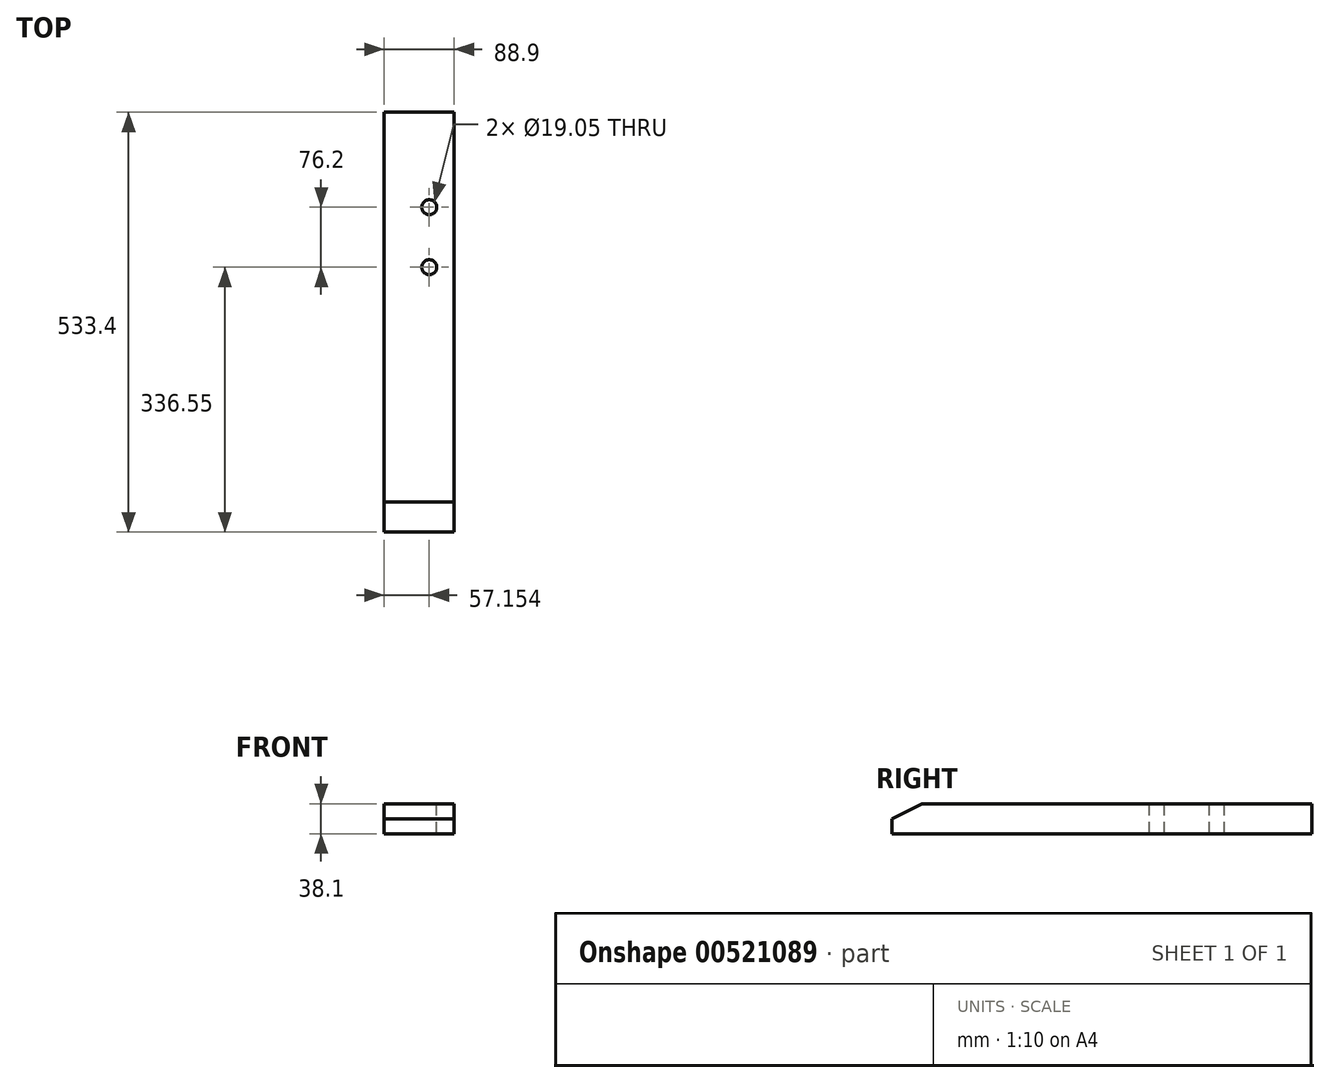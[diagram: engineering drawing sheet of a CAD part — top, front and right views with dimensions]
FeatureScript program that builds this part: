
annotation { "Feature Type Name" : "Feature", "Feature Type Description" : "" }
export const myFeature = defineFeature(function(context is Context, id is Id, definition is map)
    precondition{}
    {
        {
            var Q0;
            Q0=qCreatedBy(makeId("Front.planeOp"),FACE);
            var sketch = newSketch(context, id + "F0", { "sketchPlane" : qUnion([Q0])});
            skLineSegment(sketch, "E0.bottom", {"start": v(-42.4, -19.67) * mm, "end": v(46.5, -19.67) * mm});
            skLineSegment(sketch, "E0.top", {"start": v(-42.4, 18.43) * mm, "end": v(46.5, 18.43) * mm});
            skLineSegment(sketch, "E0.left", {"start": v(-42.4, -19.67) * mm, "end": v(-42.4, 18.43) * mm});
            skLineSegment(sketch, "E0.right", {"start": v(46.5, -19.67) * mm, "end": v(46.5, 18.43) * mm});
            skLineSegment(sketch, "E1", {"start": v(0, 43.94) * mm, "end": v(0, -47.52) * mm, "construction": true});
            skLineSegment(sketch, "E2", {"start": v(-64.12, 0) * mm, "end": v(66.16, 0) * mm, "construction": true});
            skSolve(sketch);
        }
        {
            var Q0;
            Q0=qSketchRegion(id+"F0",true);
            extrude(context, id + "F1", {"entities" : qUnion([Q0]), "endBound" : BoundingType.SYMMETRIC, "depth" : 533.4 * mm, "offsetDistance" : 25.4 * mm});
        }
        {
            var Q0;
            Q0=makeQuery(id+"F1.opExtrude","SWEPT_FACE",FACE,{"disambiguationData":[OSD([sQuery(id+"F0.wireOp",EDGE,"E0.right")])]});
            var sketch = newSketch(context, id + "F2", { "sketchPlane" : qUnion([Q0])});
            skLineSegment(sketch, "E3.0.0", {"start": v(266.7, -19.67) * mm, "end": v(266.7, 18.43) * mm});
            skLineSegment(sketch, "E3.0.1", {"start": v(266.7, 18.43) * mm, "end": v(-266.7, 18.43) * mm});
            skLineSegment(sketch, "E3.0.2", {"start": v(-266.7, 18.43) * mm, "end": v(-266.7, -19.67) * mm});
            skLineSegment(sketch, "E3.0.3", {"start": v(-266.7, -19.67) * mm, "end": v(266.7, -19.67) * mm});
            skLineSegment(sketch, "E4", {"start": v(-266.7, -0.62) * mm, "end": v(-228.6, 18.43) * mm});
            skSolve(sketch);
        }
        {
            var Q0;
            {var subQ3=sQuery(id+"F2.wireOp",EDGE,"E4");Q0=makeQuery(id+"F2.imprint","IMPRINT",FACE,{"disambiguationData":[TD([[makeQuery(id+"F2.imprint","IMPRINT",EDGE,{"derivedFrom":subQ3}),1.0]])]});}
            extrude(context, id + "F3", {"entities" : qUnion([Q0]), "operationType" : NewBodyOperationType.REMOVE, "endBound" : BoundingType.THROUGH_ALL, "oppositeDirection" : true, "depth" : 25.4 * mm, "offsetDistance" : 25.4 * mm});
        }
        {
            var Q0;
            Q0=makeQuery(id+"F1.opExtrude","SWEPT_FACE",FACE,{"disambiguationData":[OSD([sQuery(id+"F0.wireOp",EDGE,"E0.top")])]});
            var sketch = newSketch(context, id + "F4", { "sketchPlane" : qUnion([Q0])});
            skLineSegment(sketch, "E5", {"start": v(14.74, 266.7) * mm, "end": v(14.74, -228.6) * mm, "construction": true});
            skCircle(sketch, "E6", {"center": v(14.74, 146.05) * mm, "radius": 9.52 * mm});
            skCircle(sketch, "E7", {"center": v(14.74, 69.85) * mm, "radius": 9.52 * mm});
            skSolve(sketch);
        }
        {
            var Q0;
            Q0=makeQuery(id+"F4.imprint","IMPRINT",FACE,{"disambiguationData":[TD([[makeQuery(id+"F4.imprint","IMPRINT",EDGE,{"derivedFrom":sQuery(id+"F4.wireOp",EDGE,"E6")}),1.0]])]});
            var Q1;
            Q1=makeQuery(id+"F4.imprint","IMPRINT",FACE,{"disambiguationData":[TD([[makeQuery(id+"F4.imprint","IMPRINT",EDGE,{"derivedFrom":sQuery(id+"F4.wireOp",EDGE,"E7")}),1.0]])]});
            extrude(context, id + "F5", {"entities" : qUnion([Q0, Q1]), "operationType" : NewBodyOperationType.REMOVE, "endBound" : BoundingType.THROUGH_ALL, "oppositeDirection" : true, "depth" : 25.4 * mm, "offsetDistance" : 25.4 * mm});
        }
    });
